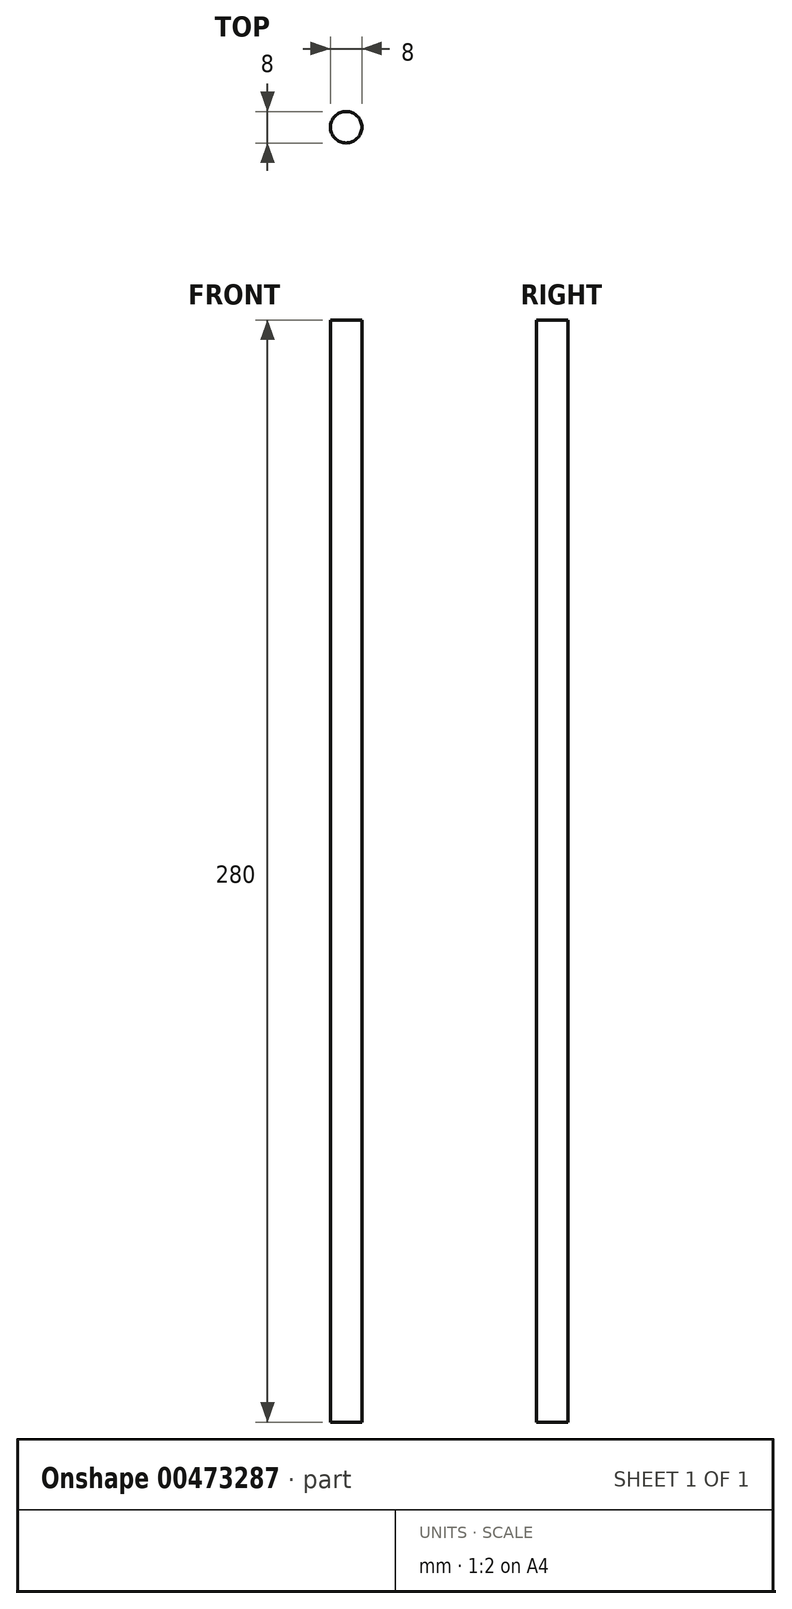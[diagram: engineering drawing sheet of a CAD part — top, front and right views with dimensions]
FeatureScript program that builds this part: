
annotation { "Feature Type Name" : "Feature", "Feature Type Description" : "" }
export const myFeature = defineFeature(function(context is Context, id is Id, definition is map)
    precondition{}
    {
        {
            var Q0;
            Q0=qCreatedBy(makeId("Top.planeOp"),FACE);
            var sketch = newSketch(context, id + "F0", { "sketchPlane" : qUnion([Q0])});
            skCircle(sketch, "E0", {"center": v(0, 0) * mm, "radius": 4 * mm});
            skSolve(sketch);
        }
        {
            var Q0;
            Q0 = qSketchRegion(id + "F0", true);
            extrude(context, id + "F1", {"entities" : qUnion([Q0]), "depth" : 280 * mm, "offsetDistance" : 25 * mm});
        }
    });
